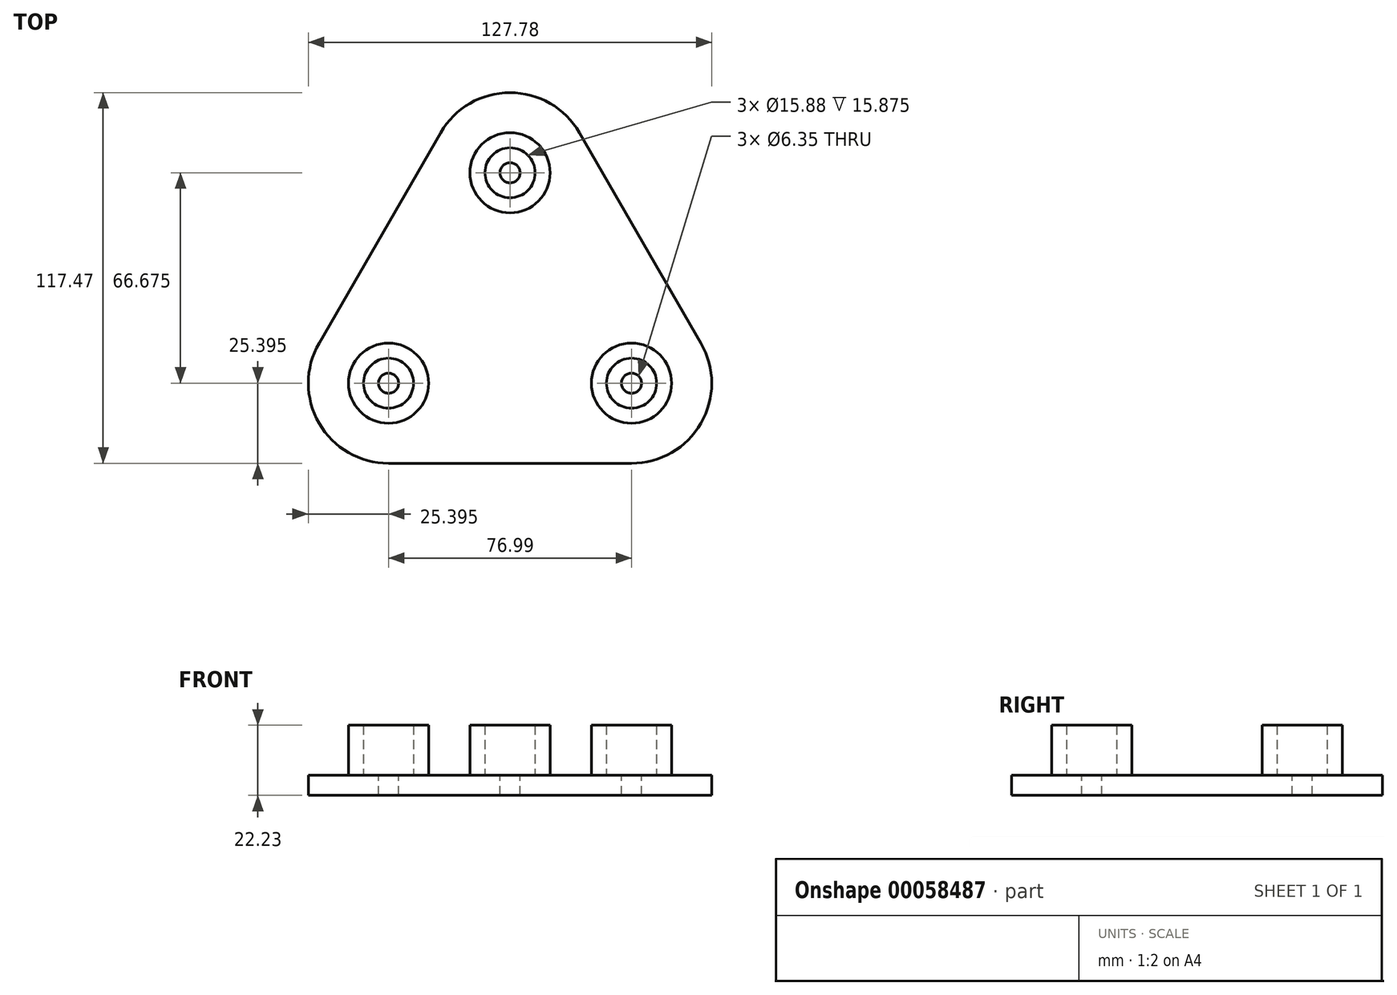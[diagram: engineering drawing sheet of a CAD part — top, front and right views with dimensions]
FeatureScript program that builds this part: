
annotation { "Feature Type Name" : "Feature", "Feature Type Description" : "" }
export const myFeature = defineFeature(function(context is Context, id is Id, definition is map)
    precondition{}
    {
        {
            var Q0;
            Q0=qCreatedBy(makeId("Top.planeOp"),FACE);
            var sketch = newSketch(context, id + "F0", { "sketchPlane" : qUnion([Q0])});
            skLineSegment(sketch, "E0", {"start": v(0, 0) * mm, "end": v(0, 36.51) * mm});
            skLineSegment(sketch, "E1", {"start": v(0, 0) * mm, "end": v(-31.62, -18.26) * mm});
            skLineSegment(sketch, "E2", {"start": v(0, 0) * mm, "end": v(31.62, -18.26) * mm});
            skCircle(sketch, "E3", {"center": v(0, 44.45) * mm, "radius": 7.94 * mm});
            skCircle(sketch, "E4", {"center": v(-38.5, -22.22) * mm, "radius": 7.94 * mm});
            skCircle(sketch, "E5", {"center": v(38.5, -22.22) * mm, "radius": 7.94 * mm});
            skArc(sketch, "E6", {"start": v(22, 57.15) * mm, "mid": v(0, 69.85) * mm, "end": v(-22, 57.15) * mm});
            skArc(sketch, "E7", {"start": v(-60.5, -9.53) * mm, "mid": v(-60.5, -34.93) * mm, "end": v(-38.5, -47.62) * mm});
            skArc(sketch, "E8", {"start": v(38.5, -47.62) * mm, "mid": v(60.5, -34.92) * mm, "end": v(60.5, -9.52) * mm});
            skLineSegment(sketch, "E9", {"start": v(-38.5, -30.16) * mm, "end": v(-38.5, -47.62) * mm});
            skLineSegment(sketch, "E10", {"start": v(-45.37, -18.26) * mm, "end": v(-60.5, -9.53) * mm});
            skLineSegment(sketch, "E11", {"start": v(38.5, -30.16) * mm, "end": v(38.5, -47.62) * mm});
            skLineSegment(sketch, "E12", {"start": v(38.5, -47.62) * mm, "end": v(-38.5, -47.62) * mm});
            skLineSegment(sketch, "E13", {"start": v(45.37, -18.26) * mm, "end": v(60.5, -9.52) * mm});
            skLineSegment(sketch, "E14", {"start": v(-6.87, 48.42) * mm, "end": v(-22, 57.15) * mm});
            skLineSegment(sketch, "E15", {"start": v(6.87, 48.42) * mm, "end": v(22, 57.15) * mm});
            skLineSegment(sketch, "E16", {"start": v(-60.5, -9.53) * mm, "end": v(-22, 57.15) * mm});
            skLineSegment(sketch, "E17", {"start": v(22, 57.15) * mm, "end": v(60.5, -9.52) * mm});
            skSolve(sketch);
        }
        {
            var Q0;
            {var subQ4=sQuery(id+"F0.wireOp",EDGE,"E0");Q0=makeQuery(id+"F0.imprint","IMPRINT",FACE,{"disambiguationData":[TD([[makeQuery(id+"F0.imprint","IMPRINT",EDGE,{"derivedFrom":subQ4}),1.0]])]});}
            var Q1;
            Q1=makeQuery(id+"F0.imprint","IMPRINT",FACE,{"disambiguationData":[TD([[makeQuery(id+"F0.imprint","IMPRINT",EDGE,{"derivedFrom":sQuery(id+"F0.wireOp",EDGE,"E7")}),1.0]])]});
            var Q2;
            {var subQ4=sQuery(id+"F0.wireOp",EDGE,"E1");Q2=makeQuery(id+"F0.imprint","IMPRINT",FACE,{"disambiguationData":[TD([[makeQuery(id+"F0.imprint","IMPRINT",EDGE,{"derivedFrom":subQ4}),1.0]])]});}
            var Q3;
            Q3=makeQuery(id+"F0.imprint","IMPRINT",FACE,{"disambiguationData":[TD([[makeQuery(id+"F0.imprint","IMPRINT",EDGE,{"derivedFrom":sQuery(id+"F0.wireOp",EDGE,"E8")}),1.0]])]});
            var Q4;
            {var subQ4=sQuery(id+"F0.wireOp",EDGE,"E0");Q4=makeQuery(id+"F0.imprint","IMPRINT",FACE,{"disambiguationData":[TD([[makeQuery(id+"F0.imprint","IMPRINT",EDGE,{"derivedFrom":subQ4}),-1.0]])]});}
            var Q5;
            Q5=makeQuery(id+"F0.imprint","IMPRINT",FACE,{"disambiguationData":[TD([[makeQuery(id+"F0.imprint","IMPRINT",EDGE,{"derivedFrom":sQuery(id+"F0.wireOp",EDGE,"E6")}),1.0]])]});
            extrude(context, id + "F1", {"entities" : qUnion([Q0, Q1, Q2, Q3, Q4, Q5]), "depth" : 6.35 * mm});
        }
        {
            var Q0;
            Q0=makeQuery(id+"F1.opExtrude","CAP_FACE",FACE,{"disambiguationData":[OSD([sQuery(id+"F0.wireOp",EDGE,"E3"),sQuery(id+"F0.wireOp",EDGE,"E4"),sQuery(id+"F0.wireOp",EDGE,"E5"),sQuery(id+"F0.wireOp",EDGE,"E6"),sQuery(id+"F0.wireOp",EDGE,"E7"),sQuery(id+"F0.wireOp",EDGE,"E8"),sQuery(id+"F0.wireOp",EDGE,"E12"),sQuery(id+"F0.wireOp",EDGE,"E16"),sQuery(id+"F0.wireOp",EDGE,"E17")])],"isStart":true});
            var sketch = newSketch(context, id + "F2", { "sketchPlane" : qUnion([Q0])});
            skCircle(sketch, "E18", {"center": v(-38.5, 22.22) * mm, "radius": 3.18 * mm});
            skCircle(sketch, "E19", {"center": v(38.5, 22.22) * mm, "radius": 3.18 * mm});
            skCircle(sketch, "E20", {"center": v(0, -44.45) * mm, "radius": 3.18 * mm});
            skSolve(sketch);
        }
        {
            var Q0;
            Q0=makeQuery(id+"F2.imprint","IMPRINT",FACE,{"disambiguationData":[TD([[makeQuery(id+"F2.imprint","IMPRINT",EDGE,{"derivedFrom":makeQuery(id+"F1.opExtrude","CAP_EDGE",EDGE,{"disambiguationData":[OSD([sQuery(id+"F0.wireOp",EDGE,"E3")])],"isStart":true})}),1.0]])]});
            var Q1;
            Q1=makeQuery(id+"F2.imprint","IMPRINT",FACE,{"disambiguationData":[TD([[makeQuery(id+"F2.imprint","IMPRINT",EDGE,{"derivedFrom":sQuery(id+"F2.wireOp",EDGE,"E18")}),-1.0]])]});
            var Q2;
            Q2=makeQuery(id+"F2.imprint","IMPRINT",FACE,{"disambiguationData":[TD([[makeQuery(id+"F2.imprint","IMPRINT",EDGE,{"derivedFrom":sQuery(id+"F2.wireOp",EDGE,"E19")}),-1.0]])]});
            var Q3;
            Q3=makeQuery(id+"F2.imprint","IMPRINT",FACE,{"disambiguationData":[TD([[makeQuery(id+"F2.imprint","IMPRINT",EDGE,{"derivedFrom":sQuery(id+"F2.wireOp",EDGE,"E20")}),-1.0]])]});
            extrude(context, id + "F3", {"entities" : qUnion([Q0, Q1, Q2, Q3]), "operationType" : NewBodyOperationType.ADD, "depth" : 6.35 * mm});
        }
        {
            var Q0;
            Q0=makeQuery(id+"F1.opExtrude","CAP_FACE",FACE,{"disambiguationData":[OSD([sQuery(id+"F0.wireOp",EDGE,"E3"),sQuery(id+"F0.wireOp",EDGE,"E4"),sQuery(id+"F0.wireOp",EDGE,"E5"),sQuery(id+"F0.wireOp",EDGE,"E6"),sQuery(id+"F0.wireOp",EDGE,"E7"),sQuery(id+"F0.wireOp",EDGE,"E8"),sQuery(id+"F0.wireOp",EDGE,"E12"),sQuery(id+"F0.wireOp",EDGE,"E16"),sQuery(id+"F0.wireOp",EDGE,"E17")])],"isStart":false});
            var sketch = newSketch(context, id + "F4", { "sketchPlane" : qUnion([Q0])});
            skCircle(sketch, "E21", {"center": v(-38.5, -22.22) * mm, "radius": 12.7 * mm});
            skCircle(sketch, "E22", {"center": v(0, 44.45) * mm, "radius": 12.7 * mm});
            skCircle(sketch, "E23", {"center": v(38.5, -22.22) * mm, "radius": 12.7 * mm});
            skSolve(sketch);
        }
        {
            var Q0;
            Q0=makeQuery(id+"F4.imprint","IMPRINT",FACE,{"disambiguationData":[TD([[makeQuery(id+"F4.imprint","IMPRINT",EDGE,{"derivedFrom":sQuery(id+"F4.wireOp",EDGE,"E21")}),-1.0]])]});
            extrude(context, id + "F5", {"entities" : qUnion([Q0]), "operationType" : NewBodyOperationType.REMOVE, "oppositeDirection" : true, "depth" : 6.35 * mm});
        }
        {
            var Q0;
            {var subQ0=sQuery(id+"F0.wireOp",EDGE,"E4");Q0=makeQuery(id+"F5.boolean.opBoolean","SPLIT",FACE,{"disambiguationData":[TD([makeQuery(id+"F1.opExtrude","SWEPT_FACE",FACE,{"disambiguationData":[OSD([subQ0])]})])],"derivedFrom":makeQuery(id+"F1.opExtrude","CAP_FACE",FACE,{"disambiguationData":[OSD([sQuery(id+"F0.wireOp",EDGE,"E3"),subQ0,sQuery(id+"F0.wireOp",EDGE,"E5"),sQuery(id+"F0.wireOp",EDGE,"E6"),sQuery(id+"F0.wireOp",EDGE,"E7"),sQuery(id+"F0.wireOp",EDGE,"E8"),sQuery(id+"F0.wireOp",EDGE,"E12"),sQuery(id+"F0.wireOp",EDGE,"E16"),sQuery(id+"F0.wireOp",EDGE,"E17")])],"isStart":false})});}
            var Q1;
            {var subQ0=sQuery(id+"F0.wireOp",EDGE,"E3");Q1=makeQuery(id+"F5.boolean.opBoolean","SPLIT",FACE,{"disambiguationData":[TD([makeQuery(id+"F1.opExtrude","SWEPT_FACE",FACE,{"disambiguationData":[OSD([subQ0])]})])],"derivedFrom":makeQuery(id+"F1.opExtrude","CAP_FACE",FACE,{"disambiguationData":[OSD([subQ0,sQuery(id+"F0.wireOp",EDGE,"E4"),sQuery(id+"F0.wireOp",EDGE,"E5"),sQuery(id+"F0.wireOp",EDGE,"E6"),sQuery(id+"F0.wireOp",EDGE,"E7"),sQuery(id+"F0.wireOp",EDGE,"E8"),sQuery(id+"F0.wireOp",EDGE,"E12"),sQuery(id+"F0.wireOp",EDGE,"E16"),sQuery(id+"F0.wireOp",EDGE,"E17")])],"isStart":false})});}
            var Q2;
            {var subQ0=sQuery(id+"F0.wireOp",EDGE,"E5");Q2=makeQuery(id+"F5.boolean.opBoolean","SPLIT",FACE,{"disambiguationData":[TD([makeQuery(id+"F1.opExtrude","SWEPT_FACE",FACE,{"disambiguationData":[OSD([subQ0])]})])],"derivedFrom":makeQuery(id+"F1.opExtrude","CAP_FACE",FACE,{"disambiguationData":[OSD([sQuery(id+"F0.wireOp",EDGE,"E3"),sQuery(id+"F0.wireOp",EDGE,"E4"),subQ0,sQuery(id+"F0.wireOp",EDGE,"E6"),sQuery(id+"F0.wireOp",EDGE,"E7"),sQuery(id+"F0.wireOp",EDGE,"E8"),sQuery(id+"F0.wireOp",EDGE,"E12"),sQuery(id+"F0.wireOp",EDGE,"E16"),sQuery(id+"F0.wireOp",EDGE,"E17")])],"isStart":false})});}
            extrude(context, id + "F6", {"entities" : qUnion([Q0, Q1, Q2]), "operationType" : NewBodyOperationType.ADD, "depth" : 9.52 * mm});
        }
    });
